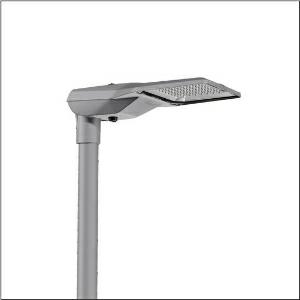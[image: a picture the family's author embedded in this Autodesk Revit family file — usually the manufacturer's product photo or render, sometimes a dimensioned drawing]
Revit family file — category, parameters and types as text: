
# Revit family: streetlight_sl_21_midi___p0_8ab_5xe3r33t08lb_8313
name_source: partatom
category: Lighting Fixtures
units: mm (PartAtom-declared; Revit-internal decimal feet)

## family parameters
Cut with Voids When Loaded = No
Host = Face
Light Source = No
Part Type = Normal
Room Calculation Point = No
Round Connector Dimension = Use Diameter
Shared = No

## types (1)
- --- (1 x LED, 12450 lm, 99.6 W, 3000K)
    Apparent Load = 100 VA
    CIE Flux Codes = 36 71 98 100 100
    Color Rendering = 70
    Color Temperature = 3000K
    Default Elevation = 1800 mm
    Description = Streetlight SL 21 midi, mast luminaire, primary light control with lens, of PMMA, primary optical cover: cover, of toughened safety glass, transparent, light distribution: P0.8aB, light emission: direct distribution, primary light characteristic: asymmetric, installation type: post-top, side-entry, LED, High Power LED, rated luminous flux: 12.450lm, luminous efficacy: 125lm/W, light colour: 730, colour temperature: 3000K, control gear: D4i, control: pre-setting: logarithmic dimming characteristic, flexible luminous flux parameterisation, time-dependent luminous flux control, constant luminous flux control, overheat protection, mains connection: 230..240V, AC, 50/60Hz, start of lifetime: 100W, end of service life: 102W, reduction: 46W, luminaire housing, of diecast aluminium, powder-coated, Siteco® metallic grey (DB 702S), corrosivity category C5 mid according to DIN EN ISO 12944, multi-level sealing system, sealing non-destructively replaceable, inclination adjustable: 0°, 5°, 10°, 15°, please order mast flange separately, length: 644mm, width: 335mm, height: 110mm, mast flange for spigot size: 42mm (side-entry): 5XC10008XM4, 60/48mm (side-entry/post-top): 5XC10108XM2, 76/60mm (side-entry/post-top): 5XC10108XM1, mounting height: 4..8m, Smart Interface below and above, protection rating (complete): IP66, insulation class (complete): insulation class II (safety insulation), certification: CE, ENEC, ENEC+, VDE, impact resistance: IK10, permissible operating ambient temperature for outdoor applications: -40..+50°C, standard-compliant lighting for roads and squares, packaging unit: 1 piece

Light Distribution: P0.8aB
    Height = 111 mm
    Lamp = 1 x LED
    Lamp Light Flux = 12450 lm
    Lamp Power = 99.6 W
    Lamp count = 1
    Length = 644 mm
    Luminous efficacy = 125 lm/W
    Manufacturer = Siteco
    ModVariant = No
    Model = 5XE3R33T08LB
    Number of Poles = 1
    OnlyDefault = Yes
    Power Factor = 1
    Product Name = Streetlight SL 21 midi | P0.8aB
    Product group = mast luminaire | pylon top
    ProductGroupID = 6100
    Protection Class = Protection class II
    Protection Degree = IP 66
    RLX_Detail_Level = 1
    RLX_Emergency_Light_Flux = 0 lm
    RLX_Emergency_Type = 0
    RLX_Emergency_Type_DB = No
    RlxData = <blob elided: 26565 chars, md5=2d3da3fa>
    Socket = socket
    Standby Power = 0 W
    System Light Flux = 12450 lm
    System Power = 100 W
    Type Comments = factory setting: luminous flux: 100 % | dim-lin: 254 | 1020 mA
    Type Image = l_1004304.jpg
    URL = http://relux.com
    VarID = @adj_033509
    Voltage = 0 V
    Weight = 0.00 kg
    Width = 336 mm

## geometry (parser evidence)
native form markers: Blend x4, Sweep x10
no freeform markers — native parametric forms only
